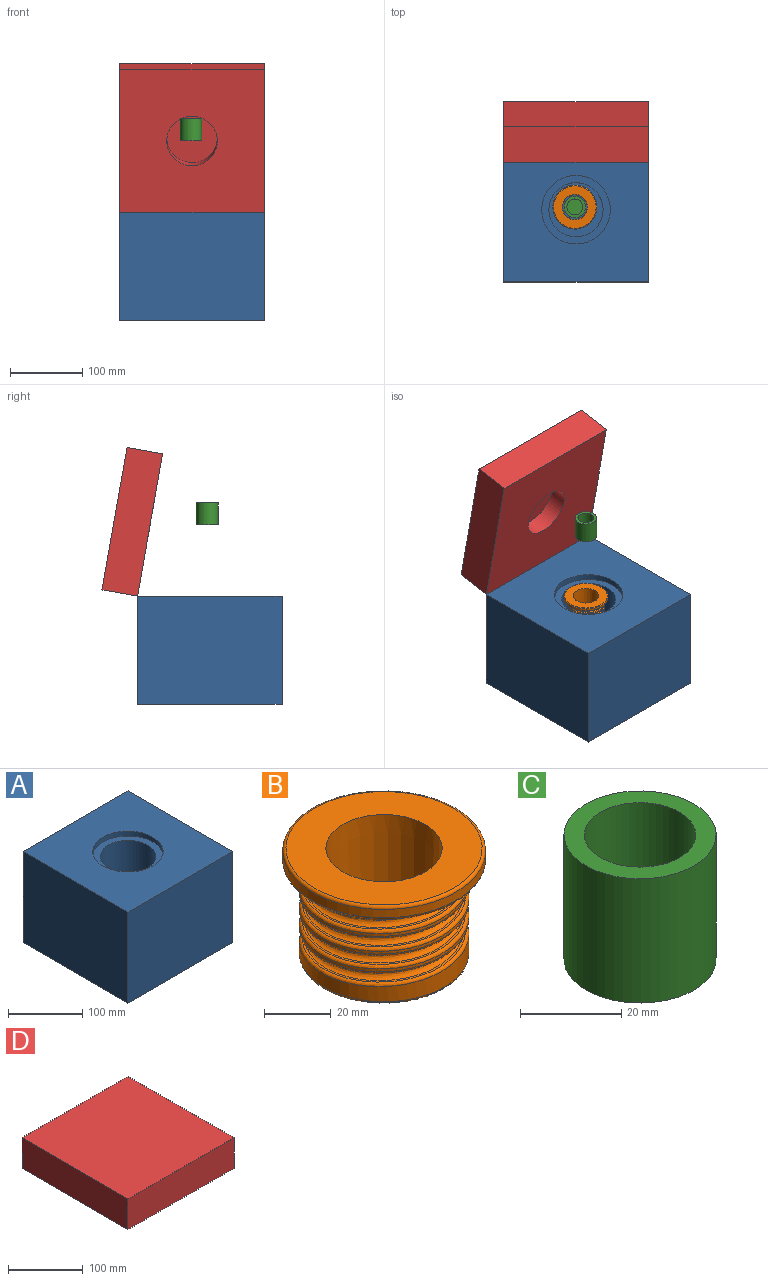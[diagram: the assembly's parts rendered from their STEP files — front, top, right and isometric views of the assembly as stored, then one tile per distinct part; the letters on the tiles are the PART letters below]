
ASSEMBLY  parts=4 mates=2
PART A: 10 faces, bbox 200x200x150 mm
  f0: plane 200x150mm, normal (-1,0,0), area 30000mm2, adj f1,f3,f4,f5
  f1: plane 200x150mm, normal (0,-1,0), area 30000mm2, adj f0,f2,f4,f5
  f2: plane 200x150mm, normal (1,0,0), area 30000mm2, adj f1,f3,f4,f5
  f3: plane 200x150mm, normal (0,1,0), area 30000mm2, adj f0,f2,f4,f5
  f4: plane 200x200mm, normal (0,0,1), area 32911.8mm2, adj f0,f1,f2,f3,f7
  f5: plane 200x200mm, normal (0,0,-1), area 40000mm2, adj f0,f1,f2,f3
  f6: plane 95x95mm, normal (0,0,1), area 2670.4mm2, adj f7,f9
  f7: cylinder r=47.5mm len=95mm, axis (0,0,1), area 2387.6mm2, adj f4,f6
  f8: plane 75x75mm, normal (0,0,1), area 4417.9mm2, adj f9
  f9: cylinder r=37.5mm len=104mm, axis (0,0,1), area 24504.4mm2, adj f6,f8
PART B: 19 faces, bbox 66.5x66.5x40.5 mm
  f0: plane 58.96x58.96mm, normal (0,0,1), area 1770.3mm2, adj f8,f16
  f1: cylinder r=30.48mm len=60.96mm, axis (0,0,-1), area 587.4mm2, adj f16,f17
  f2: cone r=25.48mm half-angle=86deg, axis (0,0,1), area 705.3mm2, adj f6,f17
  f3: cylinder r=25.48mm len=50.96mm, axis (0,0,-1), area 836.2mm2, adj f4,f10,f14,f15,f18
  f4: cylinder r=25.48mm len=50.96mm, axis (0,0,-1), area 159.9mm2, adj f3,f5,f14,f15
  f5: cylinder r=25.48mm len=50.96mm, axis (0,0,-1), area 159.9mm2, adj f4,f6,f14,f15
  f6: cylinder r=25.48mm len=50.96mm, axis (0,0,-1), area 624.2mm2, adj f2,f5,f9,f14,f15
  f7: cone r=17mm half-angle=86deg, axis (0,0,1), area 987.8mm2, adj f8,f18
  f8: cone r=17.48mm half-angle=0.7deg, axis (0,0,1), area 4333.1mm2, adj f0,f7
  f9: plane 6x4mm, normal (0,-1,0), area 11.4mm2, adj f6,f11,f12,f13,f14,f15
  f10: plane 6x4mm, normal (0,1,0), area 11.4mm2, adj f3,f11,f12,f13,f14,f15
  f11: bspline ~62.88x54.46mm, area 455.1mm2, adj f9,f10,f12,f14
  f12: bspline ~54.8x47.46mm, area 3129mm2, adj f9,f10,f11,f13
  f13: bspline ~62.88x54.46mm, area 455.1mm2, adj f9,f10,f12,f15
  f14: bspline ~50.98x50.98mm, area 992.1mm2, adj f3,f4,f5,f6,f9,f10,f11
  f15: bspline ~50.98x50.98mm, area 992.1mm2, adj f3,f4,f5,f6,f9,f10,f13
  f16: torus R=29.48mm, axis (0,0,1), area 297.2mm2, adj f0,f1
  f17: torus R=29.48mm, axis (0,0,1), area 284.3mm2, adj f1,f2
  f18: torus R=24.48mm, axis (0,0,1), area 237.1mm2, adj f3,f7
PART C: 5 faces, bbox 30x30x30 mm
  f0: plane 22x22mm, normal (0,0,1), area 380.1mm2, adj f1
  f1: cylinder r=11mm len=26mm, axis (0,0,1), area 1797mm2, adj f0,f2
  f2: plane 30x30mm, normal (0,0,1), area 326.7mm2, adj f1,f3
  f3: cylinder r=15mm len=30mm, axis (0,0,1), area 2827.4mm2, adj f2,f4
  f4: plane 30x30mm, normal (0,0,-1), area 706.9mm2, adj f3
PART D: 8 faces, bbox 200x200x50 mm
  f0: plane 200x50mm, normal (-1,0,0), area 10000mm2, adj f1,f3,f4,f5
  f1: plane 200x50mm, normal (0,-1,0), area 10000mm2, adj f0,f2,f4,f5
  f2: plane 200x50mm, normal (1,0,0), area 10000mm2, adj f1,f3,f4,f5
  f3: plane 200x50mm, normal (0,1,0), area 10000mm2, adj f0,f2,f4,f5
  f4: plane 200x200mm, normal (0,0,1), area 40000mm2, adj f0,f1,f2,f3
  f5: plane 200x200mm, normal (0,0,-1), area 36151.5mm2, adj f0,f1,f2,f3,f6
  f6: cylinder r=35mm len=70mm, axis (0,0,-1), area 5497.8mm2, adj f5,f7
  f7: plane 70x70mm, normal (0,0,-1), area 3848.5mm2, adj f6
PLACE A t=(-13.52,-78.84,-139.49)mm fixed
PLACE B t=(-15.1,-75.24,-32.49)mm
PLACE C t=(-15.1,-75.24,109.51)mm
PLACE D rot(axis=(-1,0,0),80deg) t=(-13.52,3.79,108.99)mm
MATE slider C.f1 <-> B.f1  axis (0,0,1) through (-15.1,-75.24,124.51)mm
MATE revolute A.f0 <-> D.f0  axis (1,0,0) through (-113.52,21.16,10.51)mm
